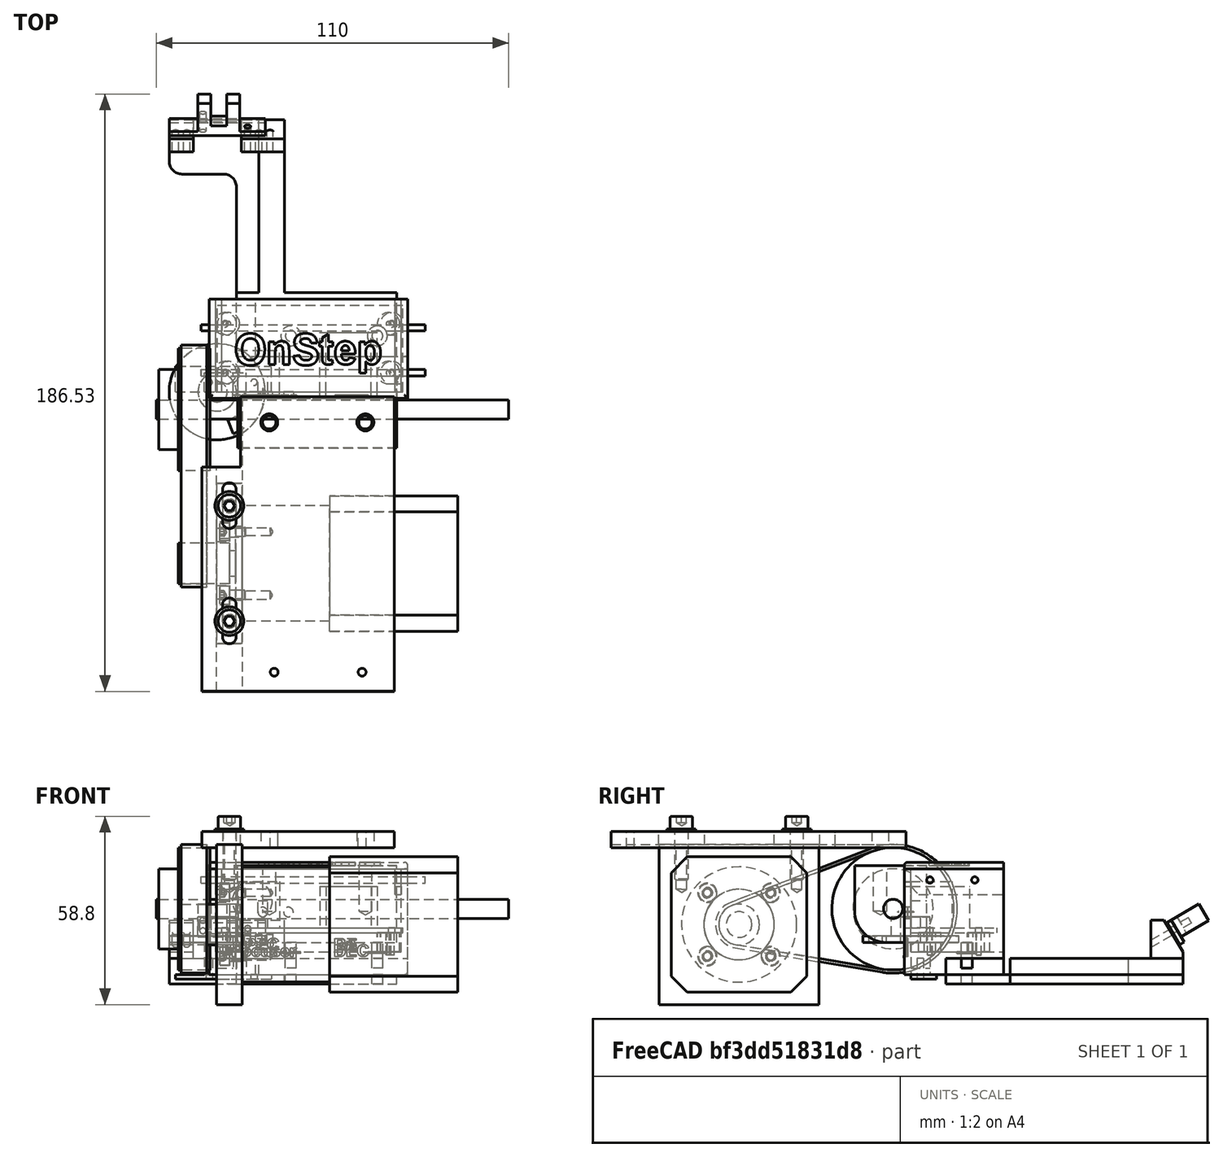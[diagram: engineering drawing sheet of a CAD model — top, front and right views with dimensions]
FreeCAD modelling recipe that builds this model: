
FCSTD DOCUMENT  (FreeCAD 0.17R13387 (Git))
Label: Onstep for Seben EQ3 v2
License: All rights reserved
LicenseURL: http://en.wikipedia.org/wiki/All_rights_reserved
objects: Part::Cylinder×107, Part::MultiFuse×65, Part::Feature×51, Part::Box×45, Part::Cut×33, Part::Part2DObjectPython×13, Part::Extrusion×13, App::Part×11, Part::Fillet×6, Part::Chamfer×2, Mesh::Feature×1
note: 335 computed .brp shape members not serialized (recipe doc carries the construction recipe); baked Part::Feature solids carry a one-line shape summary decoded from their .brp

FEATURE [Part::Feature] Part__Feature  label="Drz_1"
  Placement = pos=(-47.7402,8.35558,0) rot=(0,0,1;0rad)
  shape: bbox 74.3 x 38.2 x 38.2 mm, 17 faces (baked)
FEATURE [Part::Feature] Part__Feature001  label="Drz_2"
  Placement = pos=(55.6643,5.82,29.6) rot=(0,0,1;0rad)
  shape: bbox 60 x 92 x 5 mm, 24 faces (baked)
FEATURE [Part::Feature] Part__Feature002  label="Prir"
  Placement = pos=(17.46,-84.6049,30.6) rot=(0,1,0;3.14159rad)
  shape: bbox 8 x 50 x 50 mm, 27 faces (baked)
FEATURE [Part::Feature] Part__Feature003  label="prevod"
  Placement = pos=(35.097,-53.59,5.6) rot=(0,-1,0;1.5708rad)
  shape: bbox 87.3 x 42.3 x 42.3 mm, 26 faces (baked)
FEATURE [Part::Feature] Part__Feature004  label="remen"
  Placement = pos=(-11.203,-5.52678,10.5) rot=(0.595932,0.538266,0.595932;2.15401rad)
  shape: bbox 8 x 75.53 x 40.2 mm, 10 faces (baked)
FEATURE [Part::Feature] Part__Feature005  label="DIN 125 - A 4,3"
  Placement = pos=(3.79703,-35.59,35.4) rot=(0,1,0;1.5708rad)
  shape: bbox 9 x 9 x 0.8 mm, 4 faces (baked)
FEATURE [Part::Feature] Part__Feature006  label="DIN 125 - A 4,004"
  Placement = pos=(3.79703,-71.59,35.4) rot=(0,1,0;1.5708rad)
  shape: bbox 9 x 9 x 0.8 mm, 4 faces (baked)
FEATURE [Part::Feature] Part__Feature007  label="DIN 912 - M4 x 0,7 x 16 x 14,25"
  Placement = pos=(3.79703,-35.59,35.4) rot=(0,1,0;1.5708rad)
  shape: bbox 7.577 x 7.577 x 20 mm, 15 faces (baked)
FEATURE [Part::Feature] Part__Feature008  label="DIN 912 - M4 x 0,7 x 16 x 14,026"
  Placement = pos=(3.79703,-71.59,35.4) rot=(0,1,0;1.5708rad)
  shape: bbox 7.577 x 7.577 x 20 mm, 15 faces (baked)
FEATURE [Part::Feature] Part__Feature009  label="DIN 912 - M3 x 0,5 x 5 x 3,75"
  Placement = pos=(3.79703,-43.6905,15.4995) rot=(0,0,1;0rad)
  shape: bbox 8 x 5.953 x 5.953 mm, 15 faces (baked)
FEATURE [Part::Feature] Part__Feature010  label="DIN 912 - M3 x 0,5 x 5 x 3,076"
  Placement = pos=(3.79703,-63.4895,15.4995) rot=(1,0,0;1.5708rad)
  shape: bbox 8 x 5.953 x 5.953 mm, 15 faces (baked)
FEATURE [Part::Feature] Part__Feature011  label="DIN 912 - M3 x 0,5 x 5 x 3,077"
  Placement = pos=(3.79703,-63.4895,-4.29949) rot=(1,0,0;3.14159rad)
  shape: bbox 8 x 5.953 x 5.953 mm, 15 faces (baked)
FEATURE [Part::Feature] Part__Feature012  label="DIN 912 - M3 x 0,5 x 5 x 3,078"
  Placement = pos=(3.79703,-43.6905,-4.29949) rot=(-1,0,0;1.5708rad)
  shape: bbox 8 x 5.953 x 5.953 mm, 15 faces (baked)
FEATURE [App::Part] dalekohled1  label="DE  Motor"
  Group = -> [Part__Feature,Part__Feature001,Part__Feature002,Part__Feature003,Part__Feature004,Part__Feature005,Part__Feature006,Part__Feature007,Part__Feature008,Part__Feature009,Part__Feature010,Part__Feature011,Part__Feature012]
  License = CC BY 3.0
  LicenseURL = http://creativecommons.org/licenses/by/3.0/
  Origin = -> Origin
FEATURE [Part::Feature] Part__Feature013  label="Drz_003"
  Placement = pos=(-47.7402,8.35558,0) rot=(0,0,1;0rad)
  shape: bbox 74.3 x 38.2 x 38.2 mm, 17 faces (baked)
FEATURE [Part::Feature] Part__Feature014  label="Prir001"
  Placement = pos=(17.4566,-84.6049,30.6) rot=(0,1,0;3.14159rad)
  shape: bbox 8 x 50 x 50 mm, 27 faces (baked)
FEATURE [Part::Feature] Part__Feature015  label="Drz_004"
  Placement = pos=(55.6643,5.81614,29.6) rot=(0,0,1;0rad)
  shape: bbox 60 x 92 x 5 mm, 24 faces (baked)
FEATURE [Part::Feature] Part__Feature016  label="DIN 912 - M4 x 0,7 x 16 x 14,027"
  Placement = pos=(3.79703,-71.59,35.4) rot=(0,1,0;1.5708rad)
  shape: bbox 7.577 x 7.577 x 20 mm, 15 faces (baked)
FEATURE [Part::Feature] Part__Feature017  label="DIN 912 - M3 x 0,5 x 5 x 3,079"
  Placement = pos=(3.79703,-43.6905,15.4995) rot=(0,0,1;0rad)
  shape: bbox 8 x 5.953 x 5.953 mm, 15 faces (baked)
FEATURE [Part::Feature] Part__Feature018  label="DIN 912 - M3 x 0,5 x 5 x 3,080"
  Placement = pos=(3.79703,-63.4895,15.4995) rot=(1,0,0;1.5708rad)
  shape: bbox 8 x 5.953 x 5.953 mm, 15 faces (baked)
FEATURE [Part::Feature] Part__Feature019  label="DIN 912 - M4 x 0,7 x 16 x 14,028"
  Placement = pos=(3.79703,-35.59,35.4) rot=(0,1,0;1.5708rad)
  shape: bbox 7.577 x 7.577 x 20 mm, 15 faces (baked)
FEATURE [Part::Feature] Part__Feature020  label="DIN 912 - M3 x 0,5 x 5 x 3,081"
  Placement = pos=(3.79703,-63.4895,-4.29949) rot=(1,0,0;3.14159rad)
  shape: bbox 8 x 5.953 x 5.953 mm, 15 faces (baked)
FEATURE [Part::Feature] Part__Feature021  label="DIN 912 - M3 x 0,5 x 5 x 3,082"
  Placement = pos=(3.79703,-43.6905,-4.29949) rot=(-1,0,0;1.5708rad)
  shape: bbox 8 x 5.953 x 5.953 mm, 15 faces (baked)
FEATURE [Part::Feature] Part__Feature022  label="remen001"
  Placement = pos=(-11.203,-5.52678,10.5) rot=(0.595932,0.538266,0.595932;2.15401rad)
  shape: bbox 8 x 75.53 x 40.2 mm, 10 faces (baked)
FEATURE [Part::Feature] Part__Feature023  label="DIN 125 - A 4,005"
  Placement = pos=(3.79703,-71.59,35.4) rot=(0,1,0;1.5708rad)
  shape: bbox 9 x 9 x 0.8 mm, 4 faces (baked)
FEATURE [Part::Feature] Part__Feature024  label="prevod001"
  Placement = pos=(35.097,-53.59,5.6) rot=(0,-1,0;1.5708rad)
  shape: bbox 87.3 x 42.3 x 42.3 mm, 26 faces (baked)
FEATURE [Part::Feature] Part__Feature025  label="DIN 125 - A 4,006"
  Placement = pos=(3.79703,-35.59,35.4) rot=(0,1,0;1.5708rad)
  shape: bbox 9 x 9 x 0.8 mm, 4 faces (baked)
FEATURE [Part::Box] Box  label="borad base"
  AttacherType = Attacher::AttachEngine3D
  Height = 1.5
  Length = 58
  Width = 27
FEATURE [Part::Box] Box001  label="RJ45"
  AttacherType = Attacher::AttachEngine3D
  Height = 13
  Length = 16
  Placement = pos=(34,0,1.5) rot=(0,0,1;0rad)
  Width = 18.5
FEATURE [Part::Box] Box002  label="RJ11"
  AttacherType = Attacher::AttachEngine3D
  Height = 14.5
  Length = 13
  Placement = pos=(6.5,0,1.5) rot=(0,0,1;0rad)
  Width = 13
FEATURE [Part::Cylinder] Cylinder  label="Válec"
  Angle = 360
  AttacherType = Attacher::AttachEngine3D
  Height = 1.5
  Placement = pos=(2.5,21.25,0) rot=(0,0,1;0rad)
  Radius = 1
FEATURE [Part::Cylinder] Cylinder001  label="Válec001"
  Angle = 360
  AttacherType = Attacher::AttachEngine3D
  Height = 1.5
  Placement = pos=(2.5,6,0) rot=(0,0,1;0rad)
  Radius = 1
FEATURE [Part::Cylinder] Cylinder002  label="Válec002"
  Angle = 360
  AttacherType = Attacher::AttachEngine3D
  Height = 1.5
  Placement = pos=(54.5,21.25,0) rot=(0,0,1;0rad)
  Radius = 1
FEATURE [Part::Cylinder] Cylinder003  label="Válec003"
  Angle = 360
  AttacherType = Attacher::AttachEngine3D
  Height = 1.5
  Placement = pos=(54.5,6,0) rot=(0,0,1;0rad)
  Radius = 1
FEATURE [Part::MultiFuse] Fusion  label="diry"
  Shapes = -> [Cylinder,Cylinder001,Cylinder002,Cylinder003]
FEATURE [Part::Cut] Cut
  Base = -> Box
  Tool = -> Fusion
FEATURE [Part::MultiFuse] Fusion001  label="DE PCB face"
  Placement = pos=(0,0,3) rot=(0,0,1;0rad)
  Shapes = -> [Cut,Box001,Box002]
FEATURE [Part::Box] Box003  label="RJ046"
  AttacherType = Attacher::AttachEngine3D
  Height = 13
  Length = 16
  Placement = pos=(32,0,1.5) rot=(0,0,1;0rad)
  Width = 18.5
FEATURE [Part::Cylinder] Cylinder004  label="Válec004"
  Angle = 360
  AttacherType = Attacher::AttachEngine3D
  Height = 1.5
  Placement = pos=(54.5,21.25,0) rot=(0,0,1;0rad)
  Radius = 1
FEATURE [Part::Cylinder] Cylinder005  label="Válec005"
  Angle = 360
  AttacherType = Attacher::AttachEngine3D
  Height = 1.5
  Placement = pos=(54.5,6,0) rot=(0,0,1;0rad)
  Radius = 1
FEATURE [Part::Cylinder] Cylinder006  label="Válec006"
  Angle = 360
  AttacherType = Attacher::AttachEngine3D
  Height = 1.5
  Placement = pos=(2.5,21.25,0) rot=(0,0,1;0rad)
  Radius = 1
FEATURE [Part::Cylinder] Cylinder007  label="Válec007"
  Angle = 360
  AttacherType = Attacher::AttachEngine3D
  Height = 1.5
  Placement = pos=(2.5,6,0) rot=(0,0,1;0rad)
  Radius = 1
FEATURE [Part::MultiFuse] Fusion003  label="diry001"
  Shapes = -> [Cylinder006,Cylinder007,Cylinder004,Cylinder005]
FEATURE [Part::Box] Box005  label="borad base001"
  AttacherType = Attacher::AttachEngine3D
  Height = 1.5
  Length = 58
  Width = 27
FEATURE [Part::Cylinder] Cylinder008  label="Válec008"
  Angle = 360
  AttacherType = Attacher::AttachEngine3D
  Height = 5
  Placement = pos=(14.25,4,6.5) rot=(1,0,0;1.5708rad)
  Radius = 1.5
FEATURE [Part::Cut] Cut001
  Base = -> Box005
  Tool = -> Fusion003
FEATURE [Part::Box] Box006  label="Krychle"
  AttacherType = Attacher::AttachEngine3D
  Height = 10
  Length = 3
  Placement = pos=(12.75,0,0) rot=(0,0,1;0rad)
  Width = 5
FEATURE [Part::MultiFuse] Fusion004  label="RA PCB face"
  Placement = pos=(0,0,3) rot=(0,0,1;0rad)
  Shapes = -> [Box006,Box003,Cylinder008,Cut001]
FEATURE [Part::Cylinder] Cylinder009  label="Osa worm"
  Angle = 360
  AttacherType = Attacher::AttachEngine3D
  Height = 110
  Placement = pos=(-19,-5.5,10.5) rot=(0,1,0;1.5708rad)
  Radius = 3
FEATURE [App::Part] dalekohled002  label="RE  Motor"
  Group = -> [Part__Feature013,Part__Feature015,Part__Feature014,Part__Feature024,Part__Feature022,Part__Feature025,Part__Feature023,Part__Feature019,Part__Feature016,Part__Feature017,Part__Feature018,Part__Feature020,Part__Feature021,Cylinder009]
  License = CC BY 3.0
  LicenseURL = http://creativecommons.org/licenses/by/3.0/
  Origin = -> Origin002
FEATURE [Part::Box] Box008  label="Krychle002"
  AttacherType = Attacher::AttachEngine3D
  Height = 28
  Length = 62
  Placement = pos=(-2.5,-2,-5) rot=(0,0,1;0rad)
  Width = 31
FEATURE [Part::Box] Box009  label="Krychle003"
  AttacherType = Attacher::AttachEngine3D
  Height = 26
  Length = 58
  Placement = pos=(-0.5,0,-3) rot=(0,0,1;0rad)
  Width = 29
FEATURE [Part::Cut] Cut002  label="Základ"
  Base = -> Box008
  Tool = -> Box009
FEATURE [Part::Cylinder] Cylinder010  label="Válec009"
  Angle = 360
  AttacherType = Attacher::AttachEngine3D
  Height = 8
  Placement = pos=(53.5,21.25,0) rot=(0,0,1;0rad)
  Radius = 0.75
FEATURE [Part::Cylinder] Cylinder011  label="Válec010"
  Angle = 360
  AttacherType = Attacher::AttachEngine3D
  Height = 8
  Placement = pos=(53.5,6,0) rot=(0,0,1;0rad)
  Radius = 0.75
FEATURE [Part::Cylinder] Cylinder012  label="Válec011"
  Angle = 360
  AttacherType = Attacher::AttachEngine3D
  Height = 8
  Placement = pos=(3.5,21.25,0) rot=(0,0,1;0rad)
  Radius = 0.75
FEATURE [Part::Cylinder] Cylinder013  label="Válec012"
  Angle = 360
  AttacherType = Attacher::AttachEngine3D
  Height = 8
  Placement = pos=(3.5,6,0) rot=(0,0,1;0rad)
  Radius = 0.7
FEATURE [Part::MultiFuse] Fusion006  label="diry002"
  Placement = pos=(0,0,-4) rot=(0,0,1;0rad)
  Shapes = -> [Cylinder012,Cylinder013,Cylinder010,Cylinder011]
FEATURE [Part::Cylinder] Cylinder014  label="Válec013"
  Angle = 360
  AttacherType = Attacher::AttachEngine3D
  Height = 6.5
  Placement = pos=(53.5,6,0) rot=(0,0,1;0rad)
  Radius = 3.5
FEATURE [Part::Cylinder] Cylinder015  label="Válec014"
  Angle = 360
  AttacherType = Attacher::AttachEngine3D
  Height = 6.5
  Placement = pos=(53.5,21.25,0) rot=(0,0,1;0rad)
  Radius = 3.5
FEATURE [Part::Cylinder] Cylinder016  label="Válec015"
  Angle = 360
  AttacherType = Attacher::AttachEngine3D
  Height = 6.5
  Placement = pos=(3.5,21.25,0) rot=(0,0,1;0rad)
  Radius = 3.5
FEATURE [Part::Cylinder] Cylinder017  label="Válec016"
  Angle = 360
  AttacherType = Attacher::AttachEngine3D
  Height = 6.5
  Placement = pos=(3.5,6,0) rot=(0,0,1;0rad)
  Radius = 3.5
FEATURE [Part::MultiFuse] Fusion007  label="sloupky"
  Placement = pos=(0,0,-3.5) rot=(0,0,1;0rad)
  Shapes = -> [Cylinder016,Cylinder017,Cylinder015,Cylinder014]
FEATURE [Part::Cylinder] Cylinder018  label="Válec017"
  Angle = 360
  AttacherType = Attacher::AttachEngine3D
  Height = 8
  Placement = pos=(50,17.5,-11) rot=(0,0,1;0rad)
  Radius = 1.7
FEATURE [Part::Cylinder] Cylinder019  label="Válec018"
  Angle = 360
  AttacherType = Attacher::AttachEngine3D
  Height = 8
  Placement = pos=(23,17.5,-11) rot=(0,0,1;0rad)
  Radius = 1.7
FEATURE [Part::MultiFuse] Fusion009  label="Diry k motoru"
  Shapes = -> [Cylinder018,Cylinder019]
FEATURE [Part::Box] Box013  label="Krychle005"
  AttacherType = Attacher::AttachEngine3D
  Height = 5
  Length = 62
  Placement = pos=(-2.5,-2,-10) rot=(0,0,1;0rad)
  Width = 13
FEATURE [Part::Box] Box014  label="Krychle006"
  AttacherType = Attacher::AttachEngine3D
  Height = 5
  Length = 14.5
  Placement = pos=(-2.5,-2,-10) rot=(0,0,1;0rad)
  Width = 31
FEATURE [Part::Cylinder] Cylinder020  label="Válec019"
  Angle = 360
  AttacherType = Attacher::AttachEngine3D
  Height = 70
  Placement = pos=(-5,6,16.5) rot=(0,1,0;1.5708rad)
  Radius = 1
FEATURE [Part::Cylinder] Cylinder021  label="Válec020"
  Angle = 360
  AttacherType = Attacher::AttachEngine3D
  Height = 70
  Placement = pos=(-5,20,16.5) rot=(0,1,0;1.5708rad)
  Radius = 1
FEATURE [Part::Part2DObjectPython] ShapeString  # Draft 2D object (typed FeaturePython)
  FontFile = <path>
  Placement = pos=(15.3452,-2,30.5072) rot=(1,0,0;1.5708rad)
  Size = 4
  String = PEC
  Tracking = 0
FEATURE [Part::Extrusion] Extrude  label="Text PEC"
  Base = -> ShapeString
  Dir = (0,-1,0)
  DirMode = 2
  FaceMakerClass = Part::FaceMakerBullseye
  LengthFwd = 1
  LengthRev = 0
  Placement = pos=(-6.75,0.5,-35) rot=(0,0,1;0rad)
  Solid = false
  Symmetric = false
FEATURE [Part::Part2DObjectPython] ShapeString001  # Draft 2D object (typed FeaturePython)
  FontFile = <path>
  Placement = pos=(15.3452,-2,30.5072) rot=(1,0,0;1.5708rad)
  Size = 4
  String = RA
  Tracking = 0
FEATURE [Part::Extrusion] Extrude001  label="Text RA"
  Base = -> ShapeString001
  Dir = (0,-1,0)
  DirMode = 2
  FaceMakerClass = Part::FaceMakerBullseye
  LengthFwd = 1
  LengthRev = 0
  Placement = pos=(21,0.5,-35) rot=(0,0,1;0rad)
  Solid = false
  Symmetric = false
FEATURE [Part::Cylinder] Cylinder022  label="Válec021"
  Angle = 360
  AttacherType = Attacher::AttachEngine3D
  Height = 8
  Placement = pos=(50,17.5,-3.5) rot=(0,0,1;0rad)
  Radius = 3.1
FEATURE [Part::Cylinder] Cylinder023  label="Válec022"
  Angle = 360
  AttacherType = Attacher::AttachEngine3D
  Height = 8
  Placement = pos=(23,17.5,-3.5) rot=(0,0,1;0rad)
  Radius = 3.1
FEATURE [Part::MultiFuse] Fusion013  label="Vnitřni zahloubeni"
  Shapes = -> [Cylinder023,Cylinder022]
FEATURE [Part::Feature] Fillet001  label="DE Final solid"
  shape: bbox 62 x 31 x 33 mm, 243 faces (baked)
FEATURE [Part::Box] Box015  label="RJ049"
  AttacherType = Attacher::AttachEngine3D
  Height = 14.5
  Length = 13
  Placement = pos=(6.5,-4,4.5) rot=(0,0,1;0rad)
  Width = 13
FEATURE [Part::Cylinder] Cylinder024  label="Válec023"
  Angle = 360
  AttacherType = Attacher::AttachEngine3D
  Height = 8
  Placement = pos=(54.5,6,0) rot=(0,0,1;0rad)
  Radius = 0.75
FEATURE [Part::Cylinder] Cylinder025  label="Válec024"
  Angle = 360
  AttacherType = Attacher::AttachEngine3D
  Height = 8
  Placement = pos=(54.5,21.25,0) rot=(0,0,1;0rad)
  Radius = 0.75
FEATURE [Part::Cylinder] Cylinder026  label="Válec025"
  Angle = 360
  AttacherType = Attacher::AttachEngine3D
  Height = 8
  Placement = pos=(2.5,6,0) rot=(0,0,1;0rad)
  Radius = 0.7
FEATURE [Part::Cylinder] Cylinder027  label="Válec026"
  Angle = 360
  AttacherType = Attacher::AttachEngine3D
  Height = 6.5
  Placement = pos=(54.5,6,0) rot=(0,0,1;0rad)
  Radius = 3.5
FEATURE [Part::Cylinder] Cylinder028  label="Válec027"
  Angle = 360
  AttacherType = Attacher::AttachEngine3D
  Height = 6.5
  Placement = pos=(54.5,21.25,0) rot=(0,0,1;0rad)
  Radius = 3.5
FEATURE [Part::Cylinder] Cylinder029  label="Válec028"
  Angle = 360
  AttacherType = Attacher::AttachEngine3D
  Height = 6.5
  Placement = pos=(2.5,21.25,0) rot=(0,0,1;0rad)
  Radius = 3.5
FEATURE [Part::Cylinder] Cylinder030  label="Válec029"
  Angle = 360
  AttacherType = Attacher::AttachEngine3D
  Height = 8
  Placement = pos=(2.6,21.25,0) rot=(0,0,1;0rad)
  Radius = 0.75
FEATURE [Part::Box] Box016  label="Krychle007"
  AttacherType = Attacher::AttachEngine3D
  Height = 28
  Length = 62
  Placement = pos=(-2.5,-2,-5) rot=(0,0,1;0rad)
  Width = 31
FEATURE [Part::Box] Box017  label="RJ050"
  AttacherType = Attacher::AttachEngine3D
  Height = 13
  Length = 16
  Placement = pos=(34,-4,4.5) rot=(0,0,1;0rad)
  Width = 18.5
FEATURE [Part::Box] Box018  label="Krychle008"
  AttacherType = Attacher::AttachEngine3D
  Height = 26
  Length = 58
  Placement = pos=(-0.5,0,-3) rot=(0,0,1;0rad)
  Width = 29
FEATURE [Part::Cut] Cut013
  Base = -> Box016
  Tool = -> Box018
FEATURE [Part::Part2DObjectPython] ShapeString002  # Draft 2D object (typed FeaturePython)
  FontFile = <path>
  Placement = pos=(15.3452,-2,30.5072) rot=(1,0,0;1.5708rad)
  Size = 4
  String = Focuser
  Tracking = 0
FEATURE [Part::Part2DObjectPython] ShapeString003  # Draft 2D object (typed FeaturePython)
  FontFile = <path>
  Placement = pos=(15.3452,-2,30.5072) rot=(1,0,0;1.5708rad)
  Size = 4
  String = DEC
  Tracking = 0
FEATURE [Part::MultiFuse] Fusion016
  Shapes = -> [Box017,Box015]
FEATURE [Part::Cut] Cut014  label="RJ dirama001"
  Base = -> Cut013
  Tool = -> Fusion016
FEATURE [Part::MultiFuse] Fusion021  label="diry003"
  Placement = pos=(0,0,-4) rot=(0,0,1;0rad)
  Shapes = -> [Cylinder030,Cylinder026,Cylinder025,Cylinder024]
FEATURE [Part::Extrusion] Extrude002  label="Text DEC001"
  Base = -> ShapeString003
  Dir = (0,-1,0)
  DirMode = 2
  FaceMakerClass = Part::FaceMakerBullseye
  LengthFwd = 1
  LengthRev = 0
  Placement = pos=(21,0.5,-35) rot=(0,0,1;0rad)
  Solid = false
  Symmetric = false
FEATURE [Part::Extrusion] Extrude003  label="Text Focuser001"
  Base = -> ShapeString002
  Dir = (0,-1,0)
  DirMode = 2
  FaceMakerClass = Part::FaceMakerBullseye
  LengthFwd = 1
  LengthRev = 0
  Placement = pos=(-11,0.5,-35) rot=(0,0,1;0rad)
  Solid = false
  Symmetric = false
FEATURE [Part::MultiFuse] Fusion022  label="Texty001"
  Placement = pos=(0,0.5,0) rot=(0,0,1;0rad)
  Shapes = -> [Extrude003,Extrude002]
FEATURE [Part::Cylinder] Cylinder031  label="Válec030"
  Angle = 360
  AttacherType = Attacher::AttachEngine3D
  Height = 8
  Placement = pos=(50,17.5,-3.5) rot=(0,0,1;0rad)
  Radius = 3.1
FEATURE [Part::Cylinder] Cylinder032  label="Válec031"
  Angle = 360
  AttacherType = Attacher::AttachEngine3D
  Height = 6.5
  Placement = pos=(2.5,6,0) rot=(0,0,1;0rad)
  Radius = 3.5
FEATURE [Part::MultiFuse] Fusion015  label="sloupky001"
  Placement = pos=(0,0,-3.5) rot=(0,0,1;0rad)
  Shapes = -> [Cylinder029,Cylinder032,Cylinder028,Cylinder027]
FEATURE [Part::MultiFuse] Fusion017
  Shapes = -> [Cut014,Fusion015]
FEATURE [Part::Cut] Cut011  label="Ze sloupky001"
  Base = -> Fusion017
  Tool = -> Fusion021
FEATURE [Part::Cylinder] Cylinder033  label="Válec032"
  Angle = 360
  AttacherType = Attacher::AttachEngine3D
  Height = 70
  Placement = pos=(-5,6,16.5) rot=(0,1,0;1.5708rad)
  Radius = 1
FEATURE [Part::Cylinder] Cylinder034  label="Válec033"
  Angle = 360
  AttacherType = Attacher::AttachEngine3D
  Height = 8
  Placement = pos=(23,17.5,-3.5) rot=(0,0,1;0rad)
  Radius = 3.1
FEATURE [Part::MultiFuse] Fusion020
  Shapes = -> [Cylinder034,Cylinder031]
FEATURE [Part::Cylinder] Cylinder035  label="Válec034"
  Angle = 360
  AttacherType = Attacher::AttachEngine3D
  Height = 8
  Placement = pos=(23,17.5,-11) rot=(0,0,1;0rad)
  Radius = 1.7
FEATURE [Part::Cylinder] Cylinder036  label="Válec035"
  Angle = 360
  AttacherType = Attacher::AttachEngine3D
  Height = 8
  Placement = pos=(50,17.5,-11) rot=(0,0,1;0rad)
  Radius = 1.7
FEATURE [Part::MultiFuse] Fusion014  label="Diry k motoru001"
  Shapes = -> [Cylinder036,Cylinder035]
FEATURE [Part::Cut] Cut010
  Base = -> Cut011
  Tool = -> Fusion014
FEATURE [Part::Cylinder] Cylinder037  label="Válec036"
  Angle = 360
  AttacherType = Attacher::AttachEngine3D
  Height = 70
  Placement = pos=(-5,20,16.5) rot=(0,1,0;1.5708rad)
  Radius = 1
FEATURE [Part::MultiFuse] Fusion019  label="Horni diry001"
  Placement = pos=(0,0,3) rot=(0,0,1;0rad)
  Shapes = -> [Cylinder037,Cylinder033]
FEATURE [Part::Box] Box019  label="Krychle009"
  AttacherType = Attacher::AttachEngine3D
  Height = 5
  Length = 62
  Placement = pos=(-2.5,-2,-10) rot=(0,0,1;0rad)
  Width = 13
FEATURE [Part::Box] Box020  label="Krychle010"
  AttacherType = Attacher::AttachEngine3D
  Height = 5
  Length = 14.5
  Placement = pos=(-2.5,-2,-10) rot=(0,0,1;0rad)
  Width = 31
FEATURE [Part::MultiFuse] Fusion018  label="S dlonimy zarazkami001"
  Shapes = -> [Cut010,Box019,Box020]
FEATURE [Part::Cut] Cut015  label="Final bez napisu001"
  Base = -> Fusion018
  Tool = -> Fusion019
FEATURE [Part::Cut] Cut009  label="Z  texty001"
  Base = -> Cut015
  Tool = -> Fusion022
FEATURE [Part::Cut] Cut012
  Base = -> Cut009
  Tool = -> Fusion020
FEATURE [Part::Fillet] Fillet002  label="DE Final"
  Base = -> Cut012
  Edges = 9 edges r=1: [Edge49,Edge55,Edge265,Edge266,Edge268,Edge269,Edge271,Edge574,Edge576]
FEATURE [Part::MultiFuse] Fusion023  label="Dolni zarazky"
  Shapes = -> [Box014,Box013]
FEATURE [Part::Box] Box021  label="RJ051"
  AttacherType = Attacher::AttachEngine3D
  Height = 13
  Length = 16
  Placement = pos=(32,-5,4.5) rot=(0,0,1;0rad)
  Width = 18.5
FEATURE [Part::Cylinder] Cylinder038  label="Válec037"
  Angle = 360
  AttacherType = Attacher::AttachEngine3D
  Height = 5
  Placement = pos=(14.25,1,9.5) rot=(1,0,0;1.5708rad)
  Radius = 1.5
FEATURE [Part::MultiFuse] Fusion025  label="RJ a LED"
  Shapes = -> [Box021,Cylinder038]
FEATURE [Part::MultiFuse] Fusion027  label="texty"
  Placement = pos=(0,0.5,2) rot=(0,0,1;0rad)
  Shapes = -> [Extrude,Extrude001]
FEATURE [Part::Box] Box022  label="Krychle011"
  AttacherType = Attacher::AttachEngine3D
  Height = 2
  Length = 62
  Placement = pos=(-2.5,-2,23) rot=(0,0,1;0rad)
  Width = 31
FEATURE [Part::Box] Box023  label="Krychle012"
  AttacherType = Attacher::AttachEngine3D
  Height = 8
  Length = 58
  Placement = pos=(-0.5,0,15) rot=(0,0,1;0rad)
  Width = 29
FEATURE [Part::Box] Box024  label="Krychle013"
  AttacherType = Attacher::AttachEngine3D
  Height = 8
  Length = 54
  Placement = pos=(1.5,0,15) rot=(0,0,1;0rad)
  Width = 29
FEATURE [Part::Cylinder] Cylinder039  label="Válec038"
  Angle = 360
  AttacherType = Attacher::AttachEngine3D
  Height = 70
  Placement = pos=(-5,6,16.5) rot=(0,1,0;1.5708rad)
  Radius = 1
FEATURE [Part::Cylinder] Cylinder040  label="Válec039"
  Angle = 360
  AttacherType = Attacher::AttachEngine3D
  Height = 70
  Placement = pos=(-5,20,16.5) rot=(0,1,0;1.5708rad)
  Radius = 1
FEATURE [Part::MultiFuse] Fusion028  label="Horni diry002"
  Placement = pos=(0,0,3) rot=(0,0,1;0rad)
  Shapes = -> [Cylinder040,Cylinder039]
FEATURE [Part::MultiFuse] Fusion029
  Shapes = -> [Box022,Box023]
FEATURE [Part::MultiFuse] Fusion030
  Shapes = -> [Fusion028,Box024]
FEATURE [Part::Cut] Cut018
  Base = -> Fusion029
  Tool = -> Fusion030
FEATURE [Part::Part2DObjectPython] ShapeString004  # Draft 2D object (typed FeaturePython)
  FontFile = <path>
  Placement = pos=(15.3452,-2,30.5072) rot=(1,0,0;1.5708rad)
  Size = 10
  String = OnStep
  Tracking = 0
FEATURE [Part::Extrusion] Extrude004  label="OnStep"
  Base = -> ShapeString004
  Dir = (0,-1,0)
  DirMode = 2
  FaceMakerClass = Part::FaceMakerBullseye
  LengthFwd = 1
  LengthRev = 0
  Placement = pos=(-10,-22,22) rot=(-1,0,0;1.5708rad)
  Solid = false
  Symmetric = false
FEATURE [Part::Cut] Cut019  label="viko s texty"
  Base = -> Cut018
  Tool = -> Extrude004
FEATURE [Part::Chamfer] Chamfer
  Base = -> Cut019
  Edges = 2 edges r=2.5: [Edge355,Edge357]
FEATURE [Part::Fillet] Fillet004  label="Viko Final "
  Base = -> Chamfer
  Edges = 3 edges r=1: [Edge36,Edge38,Edge39]
FEATURE [Part::Feature] Fillet004001  label="RA Viko solid"
  shape: bbox 62 x 31 x 10 mm, 160 faces (baked)
FEATURE [Part::Feature] Fillet004002  label="DE Viko solid"
  shape: bbox 62 x 31 x 10 mm, 160 faces (baked)
FEATURE [Part::Feature] Fusion001001  label="DE PCB solid"
  shape: bbox 58 x 27 x 16 mm, 18 faces (baked)
FEATURE [App::Part] Part  label="DE 3D part"
  Group = -> [Fillet001,Fillet004002,Fusion001001]
  License = CC BY 3.0
  LicenseURL = http://creativecommons.org/licenses/by/3.0/
  Origin = -> Origin003
  Placement = pos=(68,-105,24.5) rot=(0,1,0;3.14159rad)
FEATURE [App::Part] Part002  label="DE"
  Group = -> [dalekohled1,Part]
  License = CC BY 3.0
  LicenseURL = http://creativecommons.org/licenses/by/3.0/
  Origin = -> Origin005
FEATURE [Part::Feature] Fillet004003  label="RA Final solid"
  shape: bbox 62 x 31 x 33 mm, 149 faces (baked)
FEATURE [Part::Feature] Fusion004001  label="RA PCB solid"
  shape: bbox 58 x 28 x 14.5 mm, 21 faces (baked)
FEATURE [Mesh::Feature] encoder15
FEATURE [Part::Box] Box025  label="Krychle014"
  AttacherType = Attacher::AttachEngine3D
  Height = 3
  Length = 36
  Placement = pos=(-15,11,-13) rot=(0,0,1;0rad)
  Width = 74
FEATURE [Part::Box] Box026  label="Krychle015"
  AttacherType = Attacher::AttachEngine3D
  Height = 5
  Length = 28
  Placement = pos=(-15,31,-10) rot=(0,0,1;0rad)
  Width = 54
FEATURE [Part::Box] Box027  label="Krychle016"
  AttacherType = Attacher::AttachEngine3D
  Height = 12
  Length = 36
  Placement = pos=(-15,75,-5) rot=(0,0,1;0rad)
  Width = 10
FEATURE [Part::Box] Box028  label="Krychle017"
  AttacherType = Attacher::AttachEngine3D
  Height = 3
  Length = 35
  Placement = pos=(21,11,-13) rot=(0,0,1;0rad)
  Width = 20
FEATURE [Part::Box] Box029  label="Krychle018"
  AttacherType = Attacher::AttachEngine3D
  Height = 10
  Length = 6
  Placement = pos=(0,-4,0) rot=(0,0,1;0rad)
  Width = 13
FEATURE [Part::Box] Box030  label="Krychle019"
  AttacherType = Attacher::AttachEngine3D
  Height = 8
  Length = 6
  Width = 5
FEATURE [Part::Cut] Cut020
  Base = -> Box029
  Tool = -> Box030
FEATURE [Part::Box] Box031  label="Krychle020"
  AttacherType = Attacher::AttachEngine3D
  Height = 1.5
  Length = 8
  Placement = pos=(0,-13,10) rot=(0,0,1;0rad)
  Width = 30
FEATURE [Part::Cylinder] Cylinder041  label="Válec040"
  Angle = 360
  AttacherType = Attacher::AttachEngine3D
  Height = 10
  Placement = pos=(3,-2.5,5) rot=(0,0,1;0rad)
  Radius = 1
FEATURE [Part::Cylinder] Cylinder042  label="Válec041"
  Angle = 360
  AttacherType = Attacher::AttachEngine3D
  Height = 10
  Placement = pos=(3,11.5,5) rot=(0,0,1;0rad)
  Radius = 1
FEATURE [Part::MultiFuse] Fusion004002
  Shapes = -> [Cut020,Box031]
FEATURE [Part::MultiFuse] Fusion004003
  Shapes = -> [Cylinder041,Cylinder042]
FEATURE [Part::Cut] Cut021  label="cidlo"
  Base = -> Fusion004002
  Placement = pos=(0,0,0) rot=(0.707107,0.707107,0;3.14159rad)
  Tool = -> Fusion004003
FEATURE [App::Part] Part006  label="Cidlo"
  Group = -> [Fusion004002,Fusion004003,Box029,Box031,Box030,Cylinder042,Cylinder041,Cut020,Cut021]
  License = CC BY 3.0
  LicenseURL = http://creativecommons.org/licenses/by/3.0/
  Origin = -> Origin009
  Placement = pos=(0,-9,0) rot=(0,0,1;0.523599rad)
FEATURE [Part::Chamfer] Chamfer001
  Base = -> Box027
  Edges = 1 edges: [Edge12 r1=10 r2=6]
FEATURE [Part::Cylinder] Cylinder043  label="Válec042"
  Angle = 360
  AttacherType = Attacher::AttachEngine3D
  Height = 14
  Placement = pos=(-13,74,-1) rot=(-1,0,0;1.0472rad)
  Radius = 1
FEATURE [Part::Cylinder] Cylinder044  label="Válec043"
  Angle = 360
  AttacherType = Attacher::AttachEngine3D
  Height = 14
  Placement = pos=(13,74,-1) rot=(-1,0,0;1.0472rad)
  Radius = 1
FEATURE [Part::Cylinder] Cylinder045  label="Válec044"
  Angle = 360
  AttacherType = Attacher::AttachEngine3D
  Height = 8
  Placement = pos=(50,17.5,-14) rot=(0,0,1;0rad)
  Radius = 1.7
FEATURE [Part::Cylinder] Cylinder046  label="Válec045"
  Angle = 360
  AttacherType = Attacher::AttachEngine3D
  Height = 8
  Placement = pos=(23,17.5,-14) rot=(0,0,1;0rad)
  Radius = 1.7
FEATURE [Part::MultiFuse] Fusion004007
  Shapes = -> [Box026,Box025,Box028]
FEATURE [Part::Box] Box032  label="Krychle021"
  AttacherType = Attacher::AttachEngine3D
  Height = 8
  Length = 21
  Placement = pos=(-15,11,-13) rot=(0,0,1;0rad)
  Width = 57
FEATURE [Part::Cut] Cut021002002  label="spodek"
  Base = -> Fusion004007
  Tool = -> Box032
FEATURE [Part::Box] Box034  label="Krychle023"
  AttacherType = Attacher::AttachEngine3D
  Height = 12
  Length = 15
  Placement = pos=(-7.5,75,-5) rot=(0,0,1;0rad)
  Width = 10
FEATURE [Part::Cut] Cut021002003
  Base = -> Chamfer001
  Tool = -> Box034
FEATURE [Part::MultiFuse] Fusion004008  label="Bez der001"
  Shapes = -> [Cut021002002,Cut021002003]
FEATURE [Part::Cylinder] Cylinder047  label="Válec046"
  Angle = 360
  AttacherType = Attacher::AttachEngine3D
  Height = 14
  Placement = pos=(9.5,74,-1) rot=(-1,0,0;1.0472rad)
  Radius = 1
FEATURE [Part::Cylinder] Cylinder048  label="Válec047"
  Angle = 360
  AttacherType = Attacher::AttachEngine3D
  Height = 14
  Placement = pos=(-9.5,74,-1) rot=(-1,0,0;1.0472rad)
  Radius = 1
FEATURE [Part::Cylinder] Cylinder049  label="Válec048"
  Angle = 360
  AttacherType = Attacher::AttachEngine3D
  Height = 14
  Placement = pos=(16.5,74,-1) rot=(-1,0,0;1.0472rad)
  Radius = 1
FEATURE [Part::Feature] Cut021002004  label="cidlo002"
  Placement = pos=(-2,90,12) rot=(-1,0,0;1.0472rad)
  shape: bbox 30 x 12.96 x 12.68 mm, 17 faces (baked)
FEATURE [Part::MultiFuse] Fusion004009
  Shapes = -> [Cylinder043,Cylinder044,Cylinder046,Cylinder045,Cylinder048,Cylinder047,Cylinder049]
FEATURE [Part::Cut] Cut021002005  label="plus diry"
  Base = -> Fusion004008
  Tool = -> Fusion004009
FEATURE [Part::Fillet] Fillet004005  label="PEC Holder  V2"
  Base = -> Cut021002005
  Edges = 3 edges r=4: [Edge23,Edge44,Edge65]
FEATURE [Part::Feature] Fillet004005001  label="PEC Holder  V2 solid"
  shape: bbox 71 x 74 x 20 mm, 32 faces (baked)
FEATURE [App::Part] Part001  label="RA 3D part"
  Group = -> [Fusion004001,Fillet004001,Fillet004003,Cut021002004,Fillet004005001]
  License = CC BY 3.0
  LicenseURL = http://creativecommons.org/licenses/by/3.0/
  Origin = -> Origin004
  Placement = pos=(68,-105,24.5) rot=(0,1,0;3.14159rad)
FEATURE [Part::Feature] encoder15001
  shape: bbox 32 x 31.82 x 8 mm, 660 faces, 0 solids (baked)
FEATURE [App::Part] Part003  label="RA"
  Group = -> [dalekohled002,Part001,encoder15001]
  License = CC BY 3.0
  LicenseURL = http://creativecommons.org/licenses/by/3.0/
  Origin = -> Origin006
FEATURE [Part::Cylinder] Cylinder050  label="Válec049"
  Angle = 360
  AttacherType = Attacher::AttachEngine3D
  Height = 2
  Radius = 15
FEATURE [Part::Cylinder] Cylinder051  label="Válec050"
  Angle = 16
  AttacherType = Attacher::AttachEngine3D
  Height = 2
  Radius = 14
FEATURE [Part::Cylinder] Cylinder052  label="Válec051"
  Angle = 360
  AttacherType = Attacher::AttachEngine3D
  Height = 2
  Radius = 9.5
FEATURE [Part::Cut] Cut021002006
  Base = -> Cylinder050
  Tool = -> Cylinder051
FEATURE [Part::Cylinder] Cylinder053  label="Válec052"
  Angle = 360
  AttacherType = Attacher::AttachEngine3D
  Height = 8
  Radius = 6
FEATURE [Part::MultiFuse] Fusion004010
  Shapes = -> [Cylinder053,Cylinder052,Cut021002006]
FEATURE [Part::Cylinder] Cylinder054  label="Válec053"
  Angle = 360
  AttacherType = Attacher::AttachEngine3D
  Height = 8
  Radius = 3.15
FEATURE [Part::Cut] Cut021002007  label="endoder - one pulse "
  Base = -> Fusion004010
  Placement = pos=(0,0,0) rot=(0,0,-1;1.20428rad)
  Tool = -> Cylinder054
FEATURE [App::Part] Part005  label="encoder"
  Group = -> [encoder15,Cylinder054,Fusion004010,Cylinder050,Cylinder053,Cut021002006,Cylinder052,Cylinder051,Cut021002007]
  License = CC BY 3.0
  LicenseURL = http://creativecommons.org/licenses/by/3.0/
  Origin = -> Origin008
  Placement = pos=(69,-5.5,10.5) rot=(0,1,0;-1.5708rad)
FEATURE [Part::Part2DObjectPython] ShapeString016  # Draft 2D object (typed FeaturePython)
  FontFile = <path>
  Placement = pos=(15.3452,-2,30.5072) rot=(1,0,0;1.5708rad)
  Size = 0.01
  String = .
  Tracking = 0
FEATURE [Part::Part2DObjectPython] ShapeString017  # Draft 2D object (typed FeaturePython)
  FontFile = <path>
  Placement = pos=(15.3452,-2,30.5072) rot=(1,0,0;1.5708rad)
  Size = 4
  String = DEC
  Tracking = 0
FEATURE [Part::Cylinder] Cylinder014005795  label="Válec708"
  Angle = 360
  AttacherType = Attacher::AttachEngine3D
  Height = 6.5
  Placement = pos=(53.5,6,0) rot=(0,0,1;0rad)
  Radius = 3.5
FEATURE [Part::Box] Box204  label="Krychle179"
  AttacherType = Attacher::AttachEngine3D
  Height = 28
  Length = 62
  Placement = pos=(-2.5,-2,-5) rot=(0,0,1;0rad)
  Width = 31
FEATURE [Part::Cylinder] Cylinder014005793  label="Válec706"
  Angle = 360
  AttacherType = Attacher::AttachEngine3D
  Height = 6.5
  Placement = pos=(3.5,21.25,0) rot=(0,0,1;0rad)
  Radius = 3.5
FEATURE [Part::Cylinder] Cylinder014005800  label="Válec713"
  Angle = 360
  AttacherType = Attacher::AttachEngine3D
  Height = 8
  Placement = pos=(3.5,21.25,0) rot=(0,0,1;0rad)
  Radius = 0.75
FEATURE [Part::Cylinder] Cylinder014005797  label="Válec710"
  Angle = 360
  AttacherType = Attacher::AttachEngine3D
  Height = 6.5
  Placement = pos=(53.5,21.25,0) rot=(0,0,1;0rad)
  Radius = 3.5
FEATURE [Part::Box] Box201  label="RJ056"
  AttacherType = Attacher::AttachEngine3D
  Height = 13
  Length = 16
  Placement = pos=(32,-5,4.5) rot=(0,0,1;0rad)
  Width = 18.5
FEATURE [Part::Box] Box200  label="Krychle176"
  AttacherType = Attacher::AttachEngine3D
  Height = 26
  Length = 58
  Placement = pos=(-0.5,0,-3) rot=(0,0,1;0rad)
  Width = 29
FEATURE [Part::Cut] Cut061098120  label="Základ002"
  Base = -> Box204
  Tool = -> Box200
FEATURE [Part::Cylinder] Cylinder014005798  label="Válec711"
  Angle = 360
  AttacherType = Attacher::AttachEngine3D
  Height = 8
  Placement = pos=(3.5,6,0) rot=(0,0,1;0rad)
  Radius = 0.7
FEATURE [Part::Cylinder] Cylinder014005801  label="Válec714"
  Angle = 360
  AttacherType = Attacher::AttachEngine3D
  Height = 5
  Placement = pos=(14.25,1,9.5) rot=(1,0,0;1.5708rad)
  Radius = 0.01
FEATURE [Part::Cylinder] Cylinder014005791  label="Válec704"
  Angle = 360
  AttacherType = Attacher::AttachEngine3D
  Height = 70
  Placement = pos=(-5,6,16.5) rot=(0,1,0;1.5708rad)
  Radius = 1
FEATURE [Part::Cylinder] Cylinder014005796  label="Válec709"
  Angle = 360
  AttacherType = Attacher::AttachEngine3D
  Height = 8
  Placement = pos=(53.5,6,0) rot=(0,0,1;0rad)
  Radius = 0.75
FEATURE [Part::Cylinder] Cylinder014005792  label="Válec705"
  Angle = 360
  AttacherType = Attacher::AttachEngine3D
  Height = 8
  Placement = pos=(53.5,21.25,0) rot=(0,0,1;0rad)
  Radius = 0.75
FEATURE [Part::Cylinder] Cylinder014005794  label="Válec707"
  Angle = 360
  AttacherType = Attacher::AttachEngine3D
  Height = 6.5
  Placement = pos=(3.5,6,0) rot=(0,0,1;0rad)
  Radius = 3.5
FEATURE [Part::Cylinder] Cylinder014005799  label="Válec712"
  Angle = 360
  AttacherType = Attacher::AttachEngine3D
  Height = 70
  Placement = pos=(-5,20,16.5) rot=(0,1,0;1.5708rad)
  Radius = 1
FEATURE [Part::Extrusion] Extrude086  label="Text RA002"
  Base = -> ShapeString017
  Dir = (0,-1,0)
  DirMode = 2
  FaceMakerClass = Part::FaceMakerBullseye
  LengthFwd = 1
  LengthRev = 0
  Placement = pos=(18,0.5,-33) rot=(0,0,1;0rad)
  Solid = false
  Symmetric = false
FEATURE [Part::Extrusion] Extrude087  label="Text TR002"
  Base = -> ShapeString016
  Dir = (0,-1,0)
  DirMode = 2
  FaceMakerClass = Part::FaceMakerBullseye
  LengthFwd = 1
  LengthRev = 0
  Placement = pos=(-6.75,0.5,-33) rot=(0,0,1;0rad)
  Solid = false
  Symmetric = false
FEATURE [Part::MultiFuse] Fusion001089070  label="RJ a LED002"
  Shapes = -> [Box201,Cylinder014005801]
FEATURE [Part::MultiFuse] Fusion001089075
  Shapes = -> [Extrude087,Extrude086]
FEATURE [Part::MultiFuse] Fusion001089071  label="Horni diry011"
  Placement = pos=(0,0,3) rot=(0,0,1;0rad)
  Shapes = -> [Cylinder014005799,Cylinder014005791]
FEATURE [Part::MultiFuse] Fusion001089068  label="diry017"
  Placement = pos=(0,0,-4) rot=(0,0,1;0rad)
  Shapes = -> [Cylinder014005800,Cylinder014005798,Cylinder014005792,Cylinder014005796]
FEATURE [Part::MultiFuse] Fusion001089069
  Shapes = -> [Fusion001089068,Fusion001089070,Fusion001089071]
FEATURE [Part::MultiFuse] Fusion001089072  label="sloupky005"
  Placement = pos=(0,0,-3.5) rot=(0,0,1;0rad)
  Shapes = -> [Cylinder014005793,Cylinder014005794,Cylinder014005797,Cylinder014005795]
FEATURE [Part::MultiFuse] Fusion001089074  label="bez der002"
  Shapes = -> [Cut061098120,Fusion001089072]
FEATURE [Part::Cut] Cut061098121
  Base = -> Fusion001089074
  Tool = -> Fusion001089069
FEATURE [Part::Cut] Cut061098118
  Base = -> Cut061098121
  Tool = -> Fusion001089075
FEATURE [Part::MultiFuse] Fusion024  label="Bez der"
  Shapes = -> [Fusion007,Cut002,Fusion023,Cut061098118]
FEATURE [Part::Part2DObjectPython] ShapeString018  # Draft 2D object (typed FeaturePython)
  FontFile = <path>
  Placement = pos=(15.3452,-2,30.5072) rot=(1,0,0;1.5708rad)
  Size = 0.01
  String = .
  Tracking = 0
FEATURE [Part::Part2DObjectPython] ShapeString019  # Draft 2D object (typed FeaturePython)
  FontFile = <path>
  Placement = pos=(15.3452,-2,30.5072) rot=(1,0,0;1.5708rad)
  Size = 4
  String = DEC
  Tracking = 0
FEATURE [Part::Cylinder] Cylinder014005804  label="Válec717"
  Angle = 360
  AttacherType = Attacher::AttachEngine3D
  Height = 6.5
  Placement = pos=(53.5,6,0) rot=(0,0,1;0rad)
  Radius = 3.5
FEATURE [Part::Box] Box206  label="Krychle181"
  AttacherType = Attacher::AttachEngine3D
  Height = 28
  Length = 62
  Placement = pos=(-2.5,-2,-5) rot=(0,0,1;0rad)
  Width = 31
FEATURE [Part::Cylinder] Cylinder014005805  label="Válec718"
  Angle = 360
  AttacherType = Attacher::AttachEngine3D
  Height = 6.5
  Placement = pos=(3.5,21.25,0) rot=(0,0,1;0rad)
  Radius = 3.5
FEATURE [Part::Cylinder] Cylinder014005806  label="Válec719"
  Angle = 360
  AttacherType = Attacher::AttachEngine3D
  Height = 8
  Placement = pos=(3.5,21.25,0) rot=(0,0,1;0rad)
  Radius = 0.75
FEATURE [Part::Cylinder] Cylinder014005808  label="Válec721"
  Angle = 360
  AttacherType = Attacher::AttachEngine3D
  Height = 6.5
  Placement = pos=(53.5,21.25,0) rot=(0,0,1;0rad)
  Radius = 3.5
FEATURE [Part::Box] Box208  label="RJ057"
  AttacherType = Attacher::AttachEngine3D
  Height = 13
  Length = 16
  Placement = pos=(32,-5,4.5) rot=(0,0,1;0rad)
  Width = 18.5
FEATURE [Part::Box] Box209  label="Krychle183"
  AttacherType = Attacher::AttachEngine3D
  Height = 26
  Length = 58
  Placement = pos=(-0.5,0,-3) rot=(0,0,1;0rad)
  Width = 29
FEATURE [Part::Cut] Cut061098123  label="Základ003"
  Base = -> Box206
  Tool = -> Box209
FEATURE [Part::Cylinder] Cylinder014005809  label="Válec722"
  Angle = 360
  AttacherType = Attacher::AttachEngine3D
  Height = 8
  Placement = pos=(3.5,6,0) rot=(0,0,1;0rad)
  Radius = 0.7
FEATURE [Part::Cylinder] Cylinder014005810  label="Válec723"
  Angle = 360
  AttacherType = Attacher::AttachEngine3D
  Height = 5
  Placement = pos=(14.25,1,9.5) rot=(1,0,0;1.5708rad)
  Radius = 0.01
FEATURE [Part::Cylinder] Cylinder014005812  label="Válec725"
  Angle = 360
  AttacherType = Attacher::AttachEngine3D
  Height = 70
  Placement = pos=(-5,6,16.5) rot=(0,1,0;1.5708rad)
  Radius = 1
FEATURE [Part::Cylinder] Cylinder014005813  label="Válec726"
  Angle = 360
  AttacherType = Attacher::AttachEngine3D
  Height = 8
  Placement = pos=(53.5,6,0) rot=(0,0,1;0rad)
  Radius = 0.75
FEATURE [Part::Cylinder] Cylinder014005814  label="Válec727"
  Angle = 360
  AttacherType = Attacher::AttachEngine3D
  Height = 8
  Placement = pos=(53.5,21.25,0) rot=(0,0,1;0rad)
  Radius = 0.75
FEATURE [Part::Cylinder] Cylinder014005815  label="Válec728"
  Angle = 360
  AttacherType = Attacher::AttachEngine3D
  Height = 6.5
  Placement = pos=(3.5,6,0) rot=(0,0,1;0rad)
  Radius = 3.5
FEATURE [Part::Cylinder] Cylinder014005816  label="Válec729"
  Angle = 360
  AttacherType = Attacher::AttachEngine3D
  Height = 70
  Placement = pos=(-5,20,16.5) rot=(0,1,0;1.5708rad)
  Radius = 1
FEATURE [Part::Extrusion] Extrude088  label="Text RA003"
  Base = -> ShapeString019
  Dir = (0,-1,0)
  DirMode = 2
  FaceMakerClass = Part::FaceMakerBullseye
  LengthFwd = 1
  LengthRev = 0
  Placement = pos=(18,0.5,-33) rot=(0,0,1;0rad)
  Solid = false
  Symmetric = false
FEATURE [Part::Extrusion] Extrude089  label="Text TR003"
  Base = -> ShapeString018
  Dir = (0,-1,0)
  DirMode = 2
  FaceMakerClass = Part::FaceMakerBullseye
  LengthFwd = 1
  LengthRev = 0
  Placement = pos=(-6.75,0.5,-33) rot=(0,0,1;0rad)
  Solid = false
  Symmetric = false
FEATURE [Part::MultiFuse] Fusion001089078  label="RJ a LED003"
  Shapes = -> [Box208,Cylinder014005810]
FEATURE [Part::MultiFuse] Fusion001089080
  Shapes = -> [Extrude089,Extrude088]
FEATURE [Part::MultiFuse] Fusion001089081  label="Horni diry012"
  Placement = pos=(0,0,3) rot=(0,0,1;0rad)
  Shapes = -> [Cylinder014005816,Cylinder014005812]
FEATURE [Part::MultiFuse] Fusion001089082  label="diry018"
  Placement = pos=(0,0,-4) rot=(0,0,1;0rad)
  Shapes = -> [Cylinder014005806,Cylinder014005809,Cylinder014005814,Cylinder014005813]
FEATURE [Part::MultiFuse] Fusion001089085
  Shapes = -> [Fusion001089082,Fusion001089078,Fusion001089081]
FEATURE [Part::MultiFuse] Fusion001089086  label="sloupky006"
  Placement = pos=(0,0,-3.5) rot=(0,0,1;0rad)
  Shapes = -> [Cylinder014005805,Cylinder014005815,Cylinder014005808,Cylinder014005804]
FEATURE [Part::MultiFuse] Fusion001089079  label="bez der003"
  Shapes = -> [Cut061098123,Fusion001089086]
FEATURE [Part::Cut] Cut061098124
  Base = -> Fusion001089079
  Tool = -> Fusion001089085
FEATURE [Part::Cut] Cut061098122  label="D new"
  Base = -> Cut061098124
  Tool = -> Fusion001089080
FEATURE [Part::MultiFuse] Fusion011  label="Horni diry"
  Placement = pos=(0,0,3) rot=(0,0,1;0rad)
  Shapes = -> [Cylinder021,Cylinder020,Cut061098122,Fusion009]
FEATURE [Part::MultiFuse] Fusion026  label="Diry "
  Shapes = -> [Fusion025,Fusion006,Fusion011,Fusion013]
FEATURE [Part::Cut] Cut016  label="Bez textu"
  Base = -> Fusion024
  Tool = -> Fusion026
FEATURE [Part::Cut] Cut017  label="S texty"
  Base = -> Cut016
  Tool = -> Fusion027
FEATURE [Part::Part2DObjectPython] ShapeString020  # Draft 2D object (typed FeaturePython)
  FontFile = <path>
  Placement = pos=(15.3452,-2,30.5072) rot=(1,0,0;1.5708rad)
  Size = 0.01
  String = .
  Tracking = 0
FEATURE [Part::Part2DObjectPython] ShapeString021  # Draft 2D object (typed FeaturePython)
  FontFile = <path>
  Placement = pos=(15.3452,-2,30.5072) rot=(1,0,0;1.5708rad)
  Size = 4
  String = DE
  Tracking = 0
FEATURE [Part::Extrusion] Extrude090  label="Text RA004"
  Base = -> ShapeString021
  Dir = (0,-1,0)
  DirMode = 2
  FaceMakerClass = Part::FaceMakerBullseye
  LengthFwd = 1
  LengthRev = 0
  Placement = pos=(21,0.5,-35) rot=(0,0,1;0rad)
  Solid = false
  Symmetric = false
FEATURE [Part::MultiFuse] Fusion001089094  label="texty001"
  Placement = pos=(0,0.5,2) rot=(0,0,1;0rad)
  Shapes = -> [Extrude090]
FEATURE [Part::Extrusion] Extrude091  label="Text PEC001"
  Base = -> ShapeString020
  Dir = (0,-1,0)
  DirMode = 2
  FaceMakerClass = Part::FaceMakerBullseye
  LengthFwd = 1
  LengthRev = 0
  Placement = pos=(-6.75,0.5,-35) rot=(0,0,1;0rad)
  Solid = false
  Symmetric = false
FEATURE [Part::Cylinder] Cylinder014005817  label="Válec730"
  Angle = 360
  AttacherType = Attacher::AttachEngine3D
  Height = 70
  Placement = pos=(-5,20,16.5) rot=(0,1,0;1.5708rad)
  Radius = 1
FEATURE [Part::Cylinder] Cylinder014005818  label="Válec731"
  Angle = 360
  AttacherType = Attacher::AttachEngine3D
  Height = 8
  Placement = pos=(50,17.5,-11) rot=(0,0,1;0rad)
  Radius = 1.7
FEATURE [Part::Cylinder] Cylinder014005819  label="Válec732"
  Angle = 360
  AttacherType = Attacher::AttachEngine3D
  Height = 8
  Placement = pos=(53.5,21.25,0) rot=(0,0,1;0rad)
  Radius = 0.75
FEATURE [Part::Cylinder] Cylinder014005820  label="Válec733"
  Angle = 360
  AttacherType = Attacher::AttachEngine3D
  Height = 70
  Placement = pos=(-5,6,16.5) rot=(0,1,0;1.5708rad)
  Radius = 1
FEATURE [Part::Cylinder] Cylinder014005821  label="Válec734"
  Angle = 360
  AttacherType = Attacher::AttachEngine3D
  Height = 6.5
  Placement = pos=(53.5,21.25,0) rot=(0,0,1;0rad)
  Radius = 3.5
FEATURE [Part::Cylinder] Cylinder014005822  label="Válec735"
  Angle = 360
  AttacherType = Attacher::AttachEngine3D
  Height = 8
  Placement = pos=(23,17.5,-11) rot=(0,0,1;0rad)
  Radius = 1.7
FEATURE [Part::MultiFuse] Fusion001089088  label="Diry k motoru002"
  Shapes = -> [Cylinder014005818,Cylinder014005822]
FEATURE [Part::MultiFuse] Fusion001089090  label="Horni diry013"
  Placement = pos=(0,0,3) rot=(0,0,1;0rad)
  Shapes = -> [Cylinder014005817,Cylinder014005820,Fusion001089088]
FEATURE [Part::Cylinder] Cylinder014005823  label="Válec736"
  Angle = 360
  AttacherType = Attacher::AttachEngine3D
  Height = 8
  Placement = pos=(50,17.5,-3.5) rot=(0,0,1;0rad)
  Radius = 3.1
FEATURE [Part::Box] Box210  label="Krychle184"
  AttacherType = Attacher::AttachEngine3D
  Height = 26
  Length = 58
  Placement = pos=(-0.5,0,-3) rot=(0,0,1;0rad)
  Width = 29
FEATURE [Part::Cylinder] Cylinder014005824  label="Válec737"
  Angle = 360
  AttacherType = Attacher::AttachEngine3D
  Height = 8
  Placement = pos=(3.5,6,0) rot=(0,0,1;0rad)
  Radius = 0.7
FEATURE [Part::Cylinder] Cylinder014005825  label="Válec738"
  Angle = 360
  AttacherType = Attacher::AttachEngine3D
  Height = 6.5
  Placement = pos=(3.5,21.25,0) rot=(0,0,1;0rad)
  Radius = 3.5
FEATURE [Part::Cylinder] Cylinder014005826  label="Válec739"
  Angle = 360
  AttacherType = Attacher::AttachEngine3D
  Height = 8
  Placement = pos=(23,17.5,-3.5) rot=(0,0,1;0rad)
  Radius = 3.1
FEATURE [Part::MultiFuse] Fusion001089087  label="Vnitřni zahloubeni001"
  Shapes = -> [Cylinder014005826,Cylinder014005823]
FEATURE [Part::Box] Box211  label="Krychle185"
  AttacherType = Attacher::AttachEngine3D
  Height = 5
  Length = 62
  Placement = pos=(-2.5,-2,-10) rot=(0,0,1;0rad)
  Width = 13
FEATURE [Part::Cylinder] Cylinder014005827  label="Válec740"
  Angle = 360
  AttacherType = Attacher::AttachEngine3D
  Height = 8
  Placement = pos=(3.5,21.25,0) rot=(0,0,1;0rad)
  Radius = 0.75
FEATURE [Part::Cylinder] Cylinder014005828  label="Válec741"
  Angle = 360
  AttacherType = Attacher::AttachEngine3D
  Height = 8
  Placement = pos=(53.5,6,0) rot=(0,0,1;0rad)
  Radius = 0.75
FEATURE [Part::MultiFuse] Fusion001089091  label="diry019"
  Placement = pos=(0,0,-4) rot=(0,0,1;0rad)
  Shapes = -> [Cylinder014005827,Cylinder014005824,Cylinder014005819,Cylinder014005828]
FEATURE [Part::Box] Box212  label="Krychle186"
  AttacherType = Attacher::AttachEngine3D
  Height = 5
  Length = 14.5
  Placement = pos=(-2.5,-2,-10) rot=(0,0,1;0rad)
  Width = 31
FEATURE [Part::MultiFuse] Fusion001089092  label="Dolni zarazky001"
  Shapes = -> [Box212,Box211]
FEATURE [Part::Cylinder] Cylinder014005829  label="Válec742"
  Angle = 360
  AttacherType = Attacher::AttachEngine3D
  Height = 6.5
  Placement = pos=(53.5,6,0) rot=(0,0,1;0rad)
  Radius = 3.5
FEATURE [Part::Cylinder] Cylinder014005830  label="Válec743"
  Angle = 360
  AttacherType = Attacher::AttachEngine3D
  Height = 5
  Placement = pos=(14.25,1,9.5) rot=(1,0,0;1.5708rad)
  Radius = 0.1
FEATURE [Part::Cylinder] Cylinder014005831  label="Válec744"
  Angle = 360
  AttacherType = Attacher::AttachEngine3D
  Height = 6.5
  Placement = pos=(3.5,6,0) rot=(0,0,1;0rad)
  Radius = 3.5
FEATURE [Part::MultiFuse] Fusion001089095  label="sloupky007"
  Placement = pos=(0,0,-3.5) rot=(0,0,1;0rad)
  Shapes = -> [Cylinder014005825,Cylinder014005831,Cylinder014005821,Cylinder014005829]
FEATURE [Part::Box] Box213  label="Krychle187"
  AttacherType = Attacher::AttachEngine3D
  Height = 28
  Length = 62
  Placement = pos=(-2.5,-2,-5) rot=(0,0,1;0rad)
  Width = 31
FEATURE [Part::Box] Box214  label="RJ058"
  AttacherType = Attacher::AttachEngine3D
  Height = 13
  Length = 16
  Placement = pos=(32,-5,4.5) rot=(0,0,1;0rad)
  Width = 18.5
FEATURE [Part::MultiFuse] Fusion001089093  label="Diry 001"
  Shapes = -> [Fusion001089091,Fusion001089090,Fusion001089087,Box214]
FEATURE [Part::Cut] Cut061098126  label="Základ004"
  Base = -> Box213
  Tool = -> Box210
FEATURE [Part::MultiFuse] Fusion001089096  label="Bez der002"
  Shapes = -> [Fusion001089095,Cut061098126,Fusion001089092]
FEATURE [Part::Cut] Cut061098125  label="Bez textu001"
  Base = -> Fusion001089096
  Tool = -> Fusion001089093
FEATURE [Part::Cut] Cut061098127  label="DE PCB2"
  Base = -> Cut061098125
  Tool = -> Fusion001089094
FEATURE [Part::Feature] Cut005023015001  label="GS001"
  Placement = pos=(11,38,4) rot=(0,0,1;0rad)
  shape: bbox 12.4 x 10 x 12.4 mm, 7 faces (baked)
FEATURE [Part::Part2DObjectPython] ShapeString022  # Draft 2D object (typed FeaturePython)
  FontFile = <path>
  Placement = pos=(15.3452,-2,30.5072) rot=(1,0,0;1.5708rad)
  Size = 4
  String = PEC
  Tracking = 0
FEATURE [Part::Part2DObjectPython] ShapeString023  # Draft 2D object (typed FeaturePython)
  FontFile = <path>
  Placement = pos=(15.3452,-2,30.5072) rot=(1,0,0;1.5708rad)
  Size = 4
  String = RA
  Tracking = 0
FEATURE [Part::Extrusion] Extrude092  label="Text RA005"
  Base = -> ShapeString023
  Dir = (0,-1,0)
  DirMode = 2
  FaceMakerClass = Part::FaceMakerBullseye
  LengthFwd = 1
  LengthRev = 0
  Placement = pos=(21,0.5,-35) rot=(0,0,1;0rad)
  Solid = false
  Symmetric = false
FEATURE [Part::Extrusion] Extrude093  label="Text PEC002"
  Base = -> ShapeString022
  Dir = (0,-1,0)
  DirMode = 2
  FaceMakerClass = Part::FaceMakerBullseye
  LengthFwd = 1
  LengthRev = 0
  Placement = pos=(-6.75,0.5,-35) rot=(0,0,1;0rad)
  Solid = false
  Symmetric = false
FEATURE [Part::MultiFuse] Fusion001089105  label="texty002"
  Placement = pos=(0,0.5,2) rot=(0,0,1;0rad)
  Shapes = -> [Extrude093,Extrude092]
FEATURE [Part::Box] Box215  label="Krychle188"
  AttacherType = Attacher::AttachEngine3D
  Height = 5
  Length = 62
  Placement = pos=(-2.5,-2,-10) rot=(0,0,1;0rad)
  Width = 13
FEATURE [Part::Cylinder] Cylinder014005832  label="Válec745"
  Angle = 360
  AttacherType = Attacher::AttachEngine3D
  Height = 5
  Placement = pos=(22.25,1,9.5) rot=(1,0,0;1.5708rad)
  Radius = 1.5
FEATURE [Part::Box] Box216  label="Krychle189"
  AttacherType = Attacher::AttachEngine3D
  Height = 28
  Length = 62
  Placement = pos=(-2.5,-2,-5) rot=(0,0,1;0rad)
  Width = 31
FEATURE [Part::Cylinder] Cylinder014005833  label="Válec746"
  Angle = 360
  AttacherType = Attacher::AttachEngine3D
  Height = 6.5
  Placement = pos=(53.5,6,0) rot=(0,0,1;0rad)
  Radius = 3.5
FEATURE [Part::Cylinder] Cylinder014005834  label="Válec747"
  Angle = 360
  AttacherType = Attacher::AttachEngine3D
  Height = 8
  Placement = pos=(50,17.5,-11) rot=(0,0,1;0rad)
  Radius = 1.7
FEATURE [Part::Cylinder] Cylinder014005835  label="Válec748"
  Angle = 360
  AttacherType = Attacher::AttachEngine3D
  Height = 8
  Placement = pos=(53.5,21.25,0) rot=(0,0,1;0rad)
  Radius = 0.75
FEATURE [Part::Cylinder] Cylinder014005836  label="Válec749"
  Angle = 360
  AttacherType = Attacher::AttachEngine3D
  Height = 8
  Placement = pos=(3.5,6,0) rot=(0,0,1;0rad)
  Radius = 0.7
FEATURE [Part::Cylinder] Cylinder014005837  label="Válec750"
  Angle = 360
  AttacherType = Attacher::AttachEngine3D
  Height = 8
  Placement = pos=(3.5,21.25,0) rot=(0,0,1;0rad)
  Radius = 0.75
FEATURE [Part::Box] Box217  label="Krychle190"
  AttacherType = Attacher::AttachEngine3D
  Height = 5
  Length = 14.5
  Placement = pos=(-2.5,-2,-10) rot=(0,0,1;0rad)
  Width = 31
FEATURE [Part::MultiFuse] Fusion001089101  label="Dolni zarazky002"
  Shapes = -> [Box217,Box215]
FEATURE [Part::Cylinder] Cylinder014005838  label="Válec751"
  Angle = 360
  AttacherType = Attacher::AttachEngine3D
  Height = 6.5
  Placement = pos=(53.5,21.25,0) rot=(0,0,1;0rad)
  Radius = 3.5
FEATURE [Part::Cylinder] Cylinder014005839  label="Válec752"
  Angle = 360
  AttacherType = Attacher::AttachEngine3D
  Height = 8
  Placement = pos=(23,17.5,-11) rot=(0,0,1;0rad)
  Radius = 1.7
FEATURE [Part::MultiFuse] Fusion001089098  label="Diry k motoru003"
  Shapes = -> [Cylinder014005834,Cylinder014005839]
FEATURE [Part::Cylinder] Cylinder014005840  label="Válec753"
  Angle = 360
  AttacherType = Attacher::AttachEngine3D
  Height = 70
  Placement = pos=(-5,20,16.5) rot=(0,1,0;1.5708rad)
  Radius = 1
FEATURE [Part::Cylinder] Cylinder014005841  label="Válec754"
  Angle = 360
  AttacherType = Attacher::AttachEngine3D
  Height = 70
  Placement = pos=(-5,6,16.5) rot=(0,1,0;1.5708rad)
  Radius = 1
FEATURE [Part::MultiFuse] Fusion001089103  label="Horni diry014"
  Placement = pos=(0,0,3) rot=(0,0,1;0rad)
  Shapes = -> [Cylinder014005840,Cylinder014005841,Fusion001089098]
FEATURE [Part::Cylinder] Cylinder014005842  label="Válec755"
  Angle = 360
  AttacherType = Attacher::AttachEngine3D
  Height = 6.5
  Placement = pos=(3.5,21.25,0) rot=(0,0,1;0rad)
  Radius = 3.5
FEATURE [Part::Cylinder] Cylinder014005843  label="Válec756"
  Angle = 360
  AttacherType = Attacher::AttachEngine3D
  Height = 8
  Placement = pos=(50,17.5,-3.5) rot=(0,0,1;0rad)
  Radius = 3.1
FEATURE [Part::Cylinder] Cylinder014005844  label="Válec757"
  Angle = 360
  AttacherType = Attacher::AttachEngine3D
  Height = 8
  Placement = pos=(23,17.5,-3.5) rot=(0,0,1;0rad)
  Radius = 3.1
FEATURE [Part::MultiFuse] Fusion001089097  label="Vnitřni zahloubeni002"
  Shapes = -> [Cylinder014005844,Cylinder014005843]
FEATURE [Part::Box] Box218  label="Krychle191"
  AttacherType = Attacher::AttachEngine3D
  Height = 26
  Length = 58
  Placement = pos=(-0.5,0,-3) rot=(0,0,1;0rad)
  Width = 29
FEATURE [Part::Cut] Cut005023015003  label="Základ005"
  Base = -> Box216
  Tool = -> Box218
FEATURE [Part::Cylinder] Cylinder014005845  label="Válec758"
  Angle = 360
  AttacherType = Attacher::AttachEngine3D
  Height = 8
  Placement = pos=(53.5,6,0) rot=(0,0,1;0rad)
  Radius = 0.75
FEATURE [Part::MultiFuse] Fusion001089099  label="diry020"
  Placement = pos=(0,0,-4) rot=(0,0,1;0rad)
  Shapes = -> [Cylinder014005837,Cylinder014005836,Cylinder014005835,Cylinder014005845]
FEATURE [Part::Cylinder] Cylinder014005846  label="Válec759"
  Angle = 360
  AttacherType = Attacher::AttachEngine3D
  Height = 6.5
  Placement = pos=(3.5,6,0) rot=(0,0,1;0rad)
  Radius = 3.5
FEATURE [Part::MultiFuse] Fusion001089106  label="sloupky008"
  Placement = pos=(0,0,-3.5) rot=(0,0,1;0rad)
  Shapes = -> [Cylinder014005842,Cylinder014005846,Cylinder014005838,Cylinder014005833]
FEATURE [Part::MultiFuse] Fusion001089102  label="Bez der003"
  Shapes = -> [Fusion001089106,Cut005023015003,Fusion001089101]
FEATURE [Part::Box] Box219  label="RJ059"
  AttacherType = Attacher::AttachEngine3D
  Height = 13
  Length = 16
  Placement = pos=(32,-5,4.5) rot=(0,0,1;0rad)
  Width = 18.5
FEATURE [Part::MultiFuse] Fusion001089100  label="RJ a LED005"
  Shapes = -> [Box219,Cylinder014005832,Cut005023015001]
FEATURE [Part::MultiFuse] Fusion001089104  label="Diry 002"
  Shapes = -> [Fusion001089100,Fusion001089099,Fusion001089103,Fusion001089097]
FEATURE [Part::Cut] Cut005023015004  label="Bez textu002"
  Base = -> Fusion001089102
  Tool = -> Fusion001089104
FEATURE [Part::Cut] Cut005023015002  label="RA PCB2"
  Base = -> Cut005023015004
  Tool = -> Fusion001089105
FEATURE [Part::Feature] Cut061098127001  label="DE 001"
  shape: bbox 62 x 31 x 33 mm, 86 faces (baked)
FEATURE [Part::Fillet] Fillet  label="DE MiniPCB2"
  Base = -> Cut061098127001
  Edges = 5 edges r=1: [Edge97,Edge98,Edge99,Edge100,Edge101]
FEATURE [Part::Feature] Fusion001089107  label="RA PCB solid001"
  shape: bbox 58 x 28 x 14.5 mm, 21 faces (baked)
FEATURE [App::Part] Part004  label="Working parts"
  Group = -> [Extrude004,Cut018,ShapeString004,Fusion028,Fusion030,Fusion029,Box024,Cylinder040,Box022,Box023,Cylinder039,Cut019,Chamfer,Fillet004,Extrude,Fusion009,Fusion013,Fusion007,Fusion006,Fusion011,Box008,Cylinder011,Cylinder012,Box009,Cylinder014,Cylinder010,Cylinder013,Cylinder015,Cut016,Cut017,Cut002,ShapeString001,ShapeString,Extrude001,Cylinder021,Cylinder023,Cylinder022,Cylinder016,Cylinder018,+167 more]
  License = CC BY 3.0
  LicenseURL = http://creativecommons.org/licenses/by/3.0/
  Origin = -> Origin007
FEATURE [Part::Feature] Fusion001089090001  label="Horni diry015"
  shape: bbox 70 x 16 x 28.5 mm, 12 faces, 4 solids (baked)
FEATURE [Part::Feature] Cut061098127002  label="DE 002"
  shape: bbox 62 x 31 x 33 mm, 80 faces (baked)
FEATURE [Part::Feature] Cut061098127003  label="DE 003"
  shape: bbox 62 x 31 x 33 mm, 80 faces (baked)
FEATURE [Part::Feature] Cut061098127004  label="DE 004"
  shape: bbox 62 x 31 x 33 mm, 80 faces (baked)
FEATURE [Part::Feature] Cut061098127005  label="DE 005"
  shape: bbox 62 x 31 x 33 mm, 80 faces (baked)
FEATURE [Part::Feature] Cut061098127006  label="DE 006"
  shape: bbox 62 x 31 x 33 mm, 80 faces (baked)
FEATURE [Part::Feature] Cut061098127007  label="DE 007"
  shape: bbox 62 x 31 x 33 mm, 80 faces (baked)
FEATURE [Part::Feature] Cut061098127008  label="DE 008"
  shape: bbox 62 x 31 x 33 mm, 80 faces (baked)
FEATURE [Part::Feature] Cut061098127009  label="DE 009"
  shape: bbox 62 x 31 x 33 mm, 80 faces (baked)
FEATURE [Part::Feature] Cut061098127010  label="DE 010"
  shape: bbox 62 x 31 x 33 mm, 80 faces (baked)
FEATURE [Part::Feature] Cut061098127011  label="DE 011"
  shape: bbox 62 x 31 x 33 mm, 80 faces (baked)
FEATURE [App::Part] Part007  label="kos"
  Group = -> [Cylinder014005830,ShapeString020,Extrude091,Fusion001089090001,Cut061098127002,Cut061098127003,Cut061098127004,Cut061098127005,Cut061098127006,Cut061098127007,Cut061098127008,Cut061098127009,Cut061098127010,Cut061098127011,Cut061098127001,Fillet]
  License = CC BY 3.0
  LicenseURL = http://creativecommons.org/licenses/by/3.0/
  Origin = -> Origin010
FEATURE [Part::Feature] Cut061098127012  label="DE 012"
  shape: bbox 62 x 31 x 33 mm, 80 faces (baked)
FEATURE [Part::Fillet] Fillet004005002  label="DE final"
  Base = -> Cut061098127012
  Edges = 5 edges r=1: [Edge94,Edge95,Edge96,Edge97,Edge98]
FEATURE [Part::Feature] Cut005023015002001  label="RA PCB003"
  shape: bbox 62 x 31 x 33 mm, 145 faces (baked)
FEATURE [Part::Fillet] Fillet004005003  label="RA final"
  Base = -> Cut005023015002001
  Edges = 5 edges r=1: [Edge109,Edge110,Edge111,Edge112,Edge113]
FEATURE [App::Part] Part008  label="For MiniPCB2"
  Group = -> [Cut061098127012,Fillet004005002,Cut005023015002001,Fillet004005003]
  License = CC BY 3.0
  LicenseURL = http://creativecommons.org/licenses/by/3.0/
  Origin = -> Origin011
note: 13 file-system paths scrubbed to <path> (originals preserved in the JSON sidecar)
